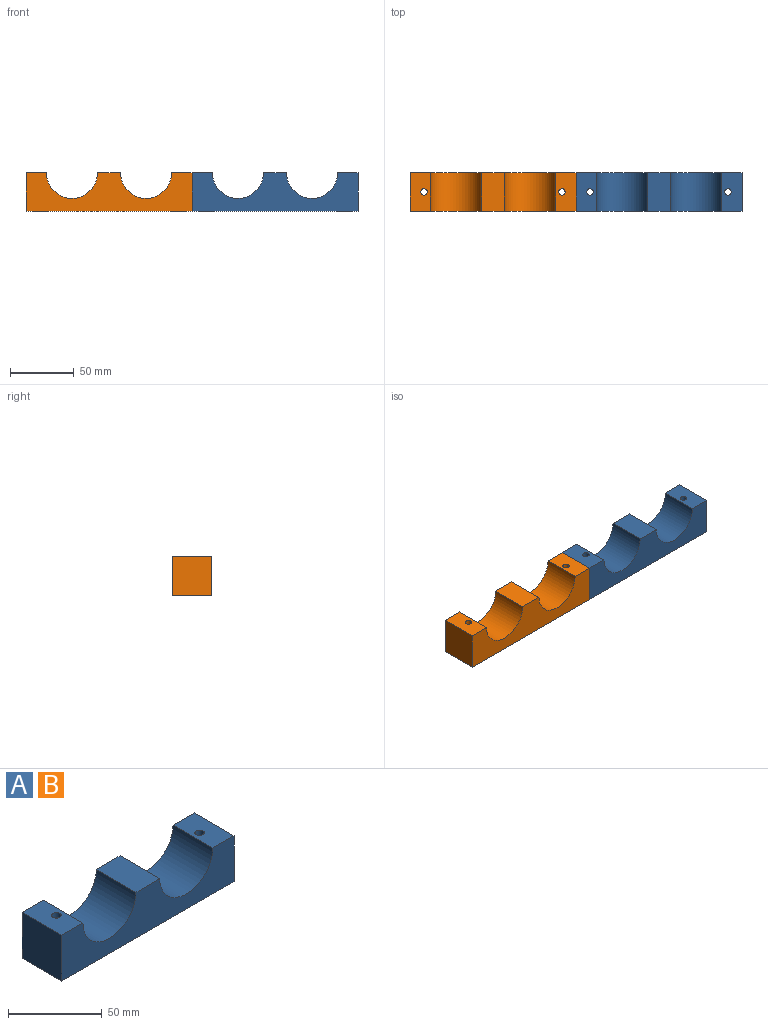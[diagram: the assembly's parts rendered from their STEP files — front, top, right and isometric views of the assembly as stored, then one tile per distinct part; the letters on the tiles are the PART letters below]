
ASSEMBLY  parts=2 mates=1
PART A: 16 faces, bbox 130x30x30 mm
  f0: plane 30x16mm, normal (0,0,1), area 460.4mm2, adj f1,f2,f4,f6,f8
  f1: plane 130x30mm, normal (0,1,0), area 2643.4mm2, adj f0,f4,f5,f7,f8,f10,f12,f14
  f2: plane 130x30mm, normal (0,-1,0), area 2643.4mm2, adj f0,f4,f5,f7,f8,f10,f12,f14
  f3: cylinder r=6mm len=12mm, axis (0,0,-1), area 188.5mm2, adj f5,f9
  f4: plane 30x30mm, normal (1,0,0), area 900mm2, adj f0,f1,f2,f5
  f5: plane 130x30mm, normal (0,0,-1), area 3673.8mm2, adj f1,f2,f3,f4,f11,f12
  f6: cylinder r=2.5mm len=20.23mm, axis (0,0,-1), area 317.8mm2, adj f0,f9
  f7: plane 30x18mm, normal (0,0,1), area 540mm2, adj f1,f2,f8,f14
  f8: cylinder r=20mm len=40mm, axis (0,1,0), area 1885mm2, adj f0,f1,f2,f7
  f9: bspline ~12x12mm, area 148.4mm2, adj f3,f6
  f10: plane 30x16mm, normal (0,0,1), area 460.4mm2, adj f1,f2,f12,f13,f14
  f11: cylinder r=6mm len=12mm, axis (0,0,-1), area 188.5mm2, adj f5,f15
  f12: plane 30x30mm, normal (-1,0,0), area 900mm2, adj f1,f2,f5,f10
  f13: cylinder r=2.5mm len=20.23mm, axis (0,0,-1), area 317.8mm2, adj f10,f15
  f14: cylinder r=20mm len=40mm, axis (0,1,0), area 1885mm2, adj f1,f2,f7,f10
  f15: bspline ~12x12mm, area 148.4mm2, adj f11,f13
PART B: same geometry as A
PLACE A rot(axis=(0,0,1),180deg) t=(93.84,-2.9,3.39)mm
PLACE B t=(-36.16,16.78,3.39)mm
MATE fastened A.f4 <-> B.f4  axis (-1,0,0) through (28.84,6.94,18.39)mm
